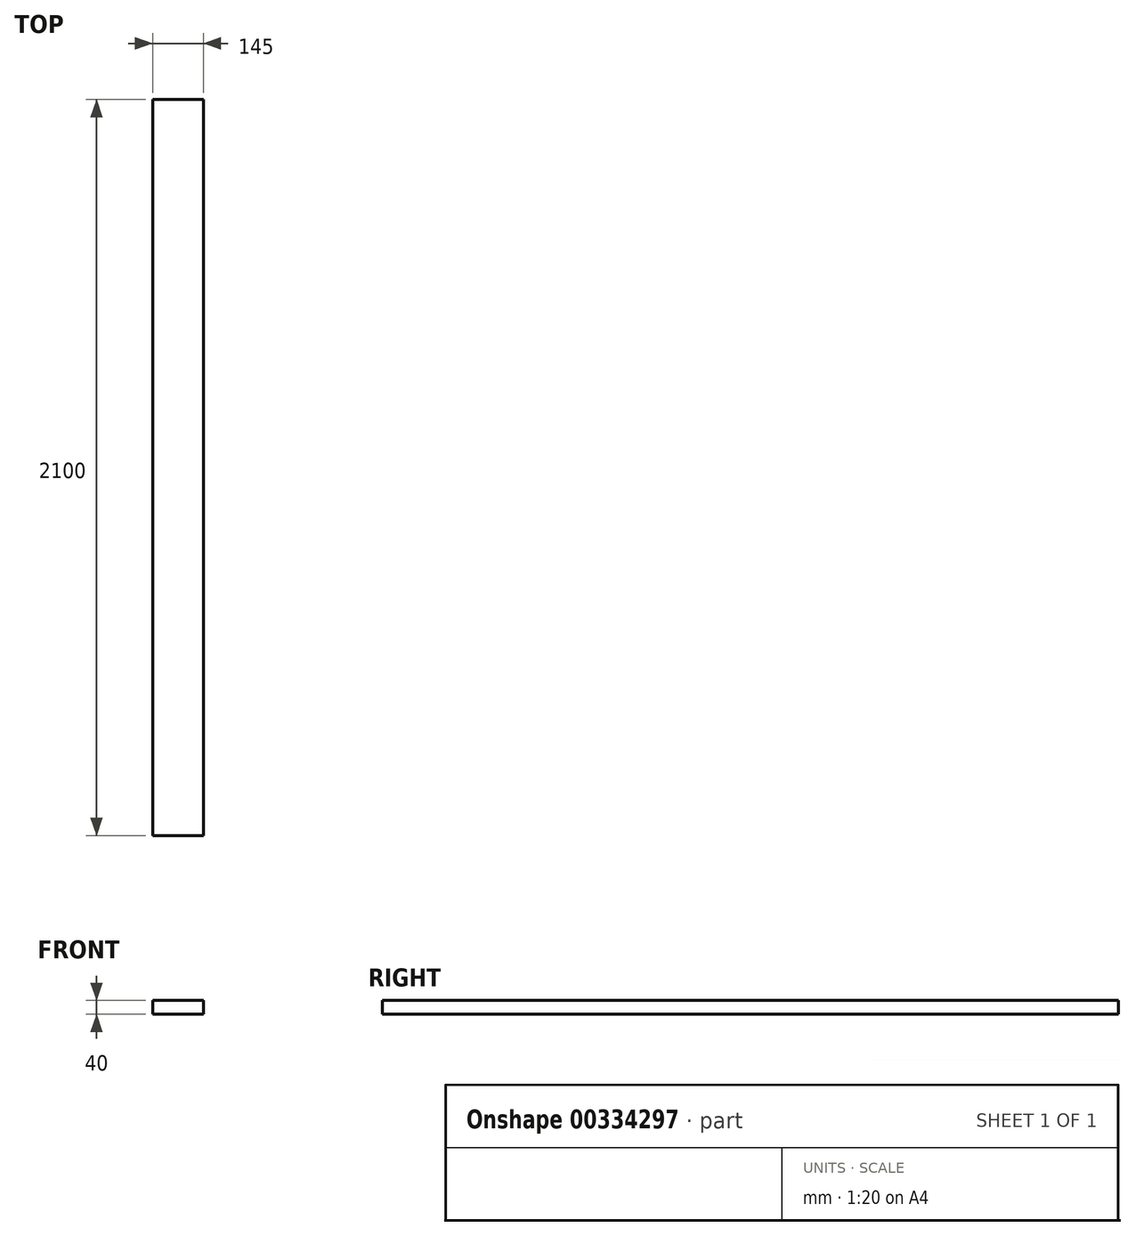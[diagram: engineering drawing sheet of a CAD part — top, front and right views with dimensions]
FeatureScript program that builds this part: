
annotation { "Feature Type Name" : "Feature", "Feature Type Description" : "" }
export const myFeature = defineFeature(function(context is Context, id is Id, definition is map)
    precondition{}
    {
        {
            var Q0;
            Q0=qCreatedBy(makeId("Front.planeOp"),FACE);
            var sketch = newSketch(context, id + "F0", { "sketchPlane" : qUnion([Q0])});
            skLineSegment(sketch, "E0.bottom", {"start": v(75.78, 20) * mm, "end": v(-69.22, 20) * mm});
            skLineSegment(sketch, "E0.top", {"start": v(75.78, -20) * mm, "end": v(-69.22, -20) * mm});
            skLineSegment(sketch, "E0.left", {"start": v(75.78, 20) * mm, "end": v(75.78, -20) * mm});
            skLineSegment(sketch, "E0.right", {"start": v(-69.22, 20) * mm, "end": v(-69.22, -20) * mm});
            skPoint(sketch, "E0.middle", {"position": v(3.28, 0) * mm});
            skSolve(sketch);
        }
        {
            var Q0;
            Q0=makeQuery(id+"F0.imprint","IMPRINT",FACE,{"disambiguationData":[TD([[makeQuery(id+"F0.imprint","IMPRINT",EDGE,{"derivedFrom":sQuery(id+"F0.wireOp",EDGE,"E0.bottom")}),1.0]])]});
            extrude(context, id + "F1", {"entities" : qUnion([Q0]), "oppositeDirection" : true, "depth" : 2100 * mm});
        }
    });
